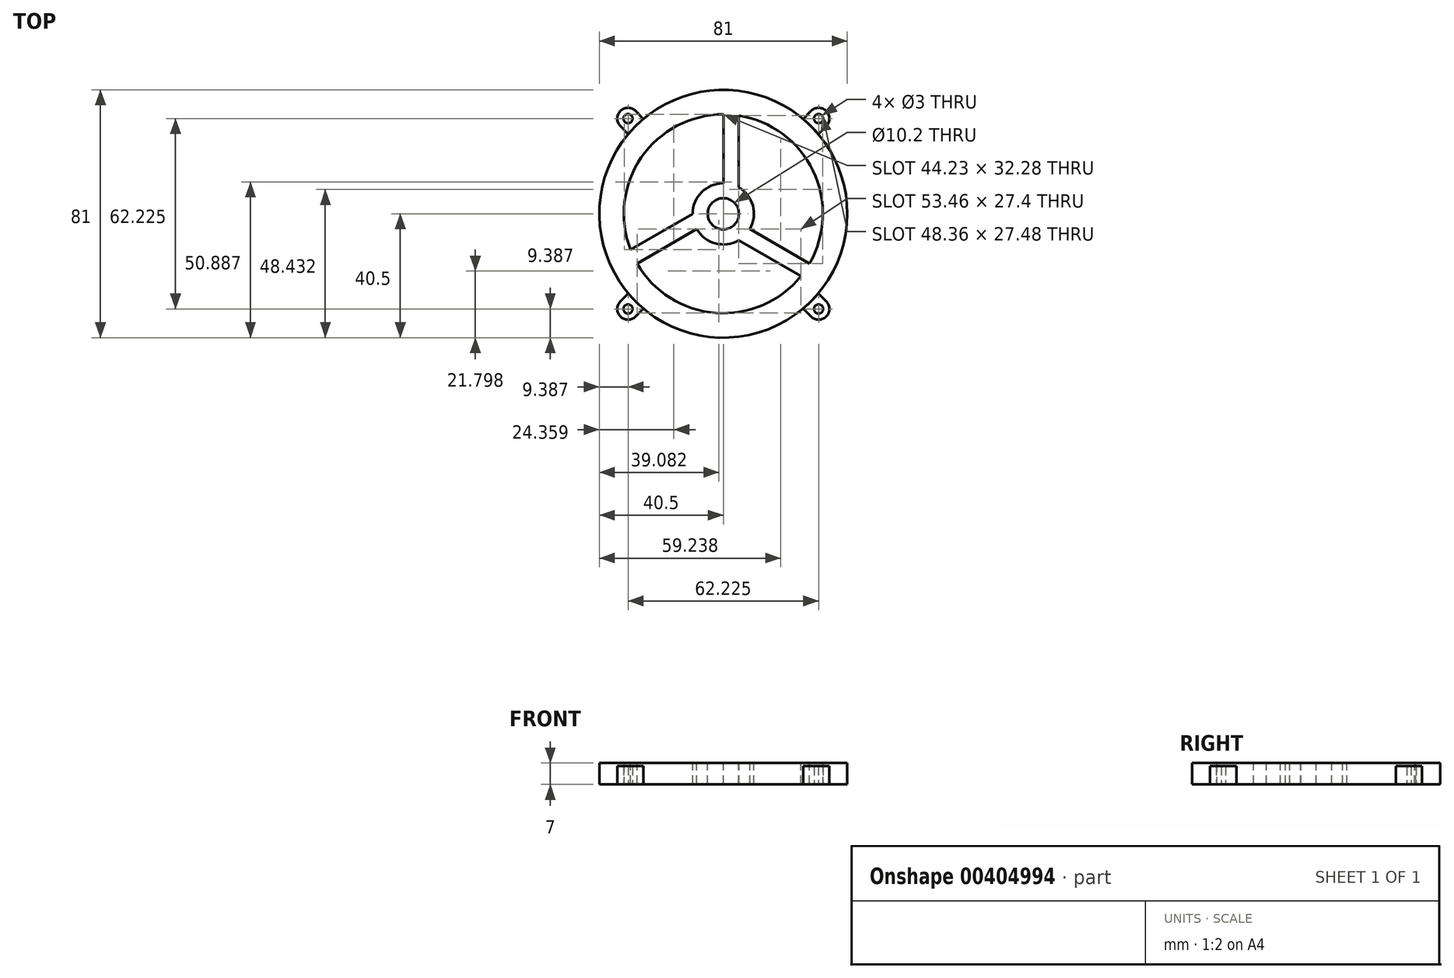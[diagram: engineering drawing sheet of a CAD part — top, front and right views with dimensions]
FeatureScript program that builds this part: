
annotation { "Feature Type Name" : "Feature", "Feature Type Description" : "" }
export const myFeature = defineFeature(function(context is Context, id is Id, definition is map)
    precondition{}
    {
        {
            var Q0;
            Q0=qCreatedBy(makeId("Top.planeOp"),FACE);
            var sketch = newSketch(context, id + "F0", { "sketchPlane" : qUnion([Q0])});
            skCircle(sketch, "E0", {"center": v(0, 0) * mm, "radius": 37 * mm});
            skCircle(sketch, "E1", {"center": v(0, 0) * mm, "radius": 32.5 * mm});
            skCircle(sketch, "E2", {"center": v(0, 0) * mm, "radius": 40.5 * mm});
            skLineSegment(sketch, "E3", {"start": v(0, 0) * mm, "end": v(-31.11, 31.11) * mm, "construction": true});
            skCircle(sketch, "E4", {"center": v(-31.11, 31.11) * mm, "radius": 1.5 * mm});
            skArc(sketch, "E5", {"start": v(-28.64, 33.59) * mm, "mid": v(-33.59, 33.59) * mm, "end": v(-33.59, 28.64) * mm});
            skLineSegment(sketch, "E6", {"start": v(-33.59, 28.64) * mm, "end": v(-31, 26.06) * mm});
            skLineSegment(sketch, "E7", {"start": v(-28.64, 33.59) * mm, "end": v(-26.06, 31) * mm});
            skLineSegment(sketch, "E8.1.0", {"start": v(-33.59, -28.64) * mm, "end": v(-31, -26.06) * mm});
            skCircle(sketch, "E8.1.1", {"center": v(-31.11, -31.11) * mm, "radius": 1.5 * mm});
            skArc(sketch, "E8.1.2", {"start": v(-33.59, -28.64) * mm, "mid": v(-33.59, -33.59) * mm, "end": v(-28.64, -33.59) * mm});
            skLineSegment(sketch, "E8.1.3", {"start": v(-28.64, -33.59) * mm, "end": v(-26.06, -31) * mm});
            skLineSegment(sketch, "E8.2.0", {"start": v(28.64, -33.59) * mm, "end": v(26.06, -31) * mm});
            skCircle(sketch, "E8.2.1", {"center": v(31.11, -31.11) * mm, "radius": 1.5 * mm});
            skArc(sketch, "E8.2.2", {"start": v(28.64, -33.59) * mm, "mid": v(33.59, -33.59) * mm, "end": v(33.59, -28.64) * mm});
            skLineSegment(sketch, "E8.2.3", {"start": v(33.59, -28.64) * mm, "end": v(31, -26.06) * mm});
            skLineSegment(sketch, "E8.3.0", {"start": v(33.59, 28.64) * mm, "end": v(31, 26.06) * mm});
            skCircle(sketch, "E8.3.1", {"center": v(31.11, 31.11) * mm, "radius": 1.5 * mm});
            skArc(sketch, "E8.3.2", {"start": v(33.59, 28.64) * mm, "mid": v(33.59, 33.59) * mm, "end": v(28.64, 33.59) * mm});
            skLineSegment(sketch, "E8.3.3", {"start": v(28.64, 33.59) * mm, "end": v(26.06, 31) * mm});
            skSolve(sketch);
        }
        {
            var Q0;
            Q0=makeQuery(id+"F0.imprint","IMPRINT",FACE,{"disambiguationData":[TD([[makeQuery(id+"F0.imprint","IMPRINT",EDGE,{"derivedFrom":sQuery(id+"F0.wireOp",EDGE,"E0")}),-1.0]])]});
            extrude(context, id + "F1", {"entities" : qUnion([Q0]), "depth" : 7 * mm});
        }
        {
            var Q0;
            {var subQ0=sQuery(id+"F0.wireOp",EDGE,"E8.1.0");Q0=makeQuery(id+"F0.imprint","IMPRINT",FACE,{"disambiguationData":[TD([[makeQuery(id+"F0.imprint","IMPRINT",EDGE,{"derivedFrom":subQ0}),-1.0]])]});}
            var Q1;
            {var subQ1=sQuery(id+"F0.wireOp",EDGE,"E8.2.0");Q1=makeQuery(id+"F0.imprint","IMPRINT",FACE,{"disambiguationData":[TD([[makeQuery(id+"F0.imprint","IMPRINT",EDGE,{"derivedFrom":subQ1}),-1.0]])]});}
            var Q2;
            {var subQ0=sQuery(id+"F0.wireOp",EDGE,"E8.3.0");Q2=makeQuery(id+"F0.imprint","IMPRINT",FACE,{"disambiguationData":[TD([[makeQuery(id+"F0.imprint","IMPRINT",EDGE,{"derivedFrom":subQ0}),-1.0]])]});}
            var Q3;
            Q3=makeQuery(id+"F0.imprint","IMPRINT",FACE,{"disambiguationData":[TD([[makeQuery(id+"F0.imprint","IMPRINT",EDGE,{"derivedFrom":sQuery(id+"F0.wireOp",EDGE,"E4")}),-1.0]])]});
            extrude(context, id + "F2", {"entities" : qUnion([Q0, Q1, Q2, Q3]), "operationType" : NewBodyOperationType.ADD, "depth" : 6 * mm});
        }
        {
            var Q0;
            Q0=makeQuery(id+"F0.imprint","IMPRINT",FACE,{"disambiguationData":[TD([[makeQuery(id+"F0.imprint","IMPRINT",EDGE,{"derivedFrom":sQuery(id+"F0.wireOp",EDGE,"E0")}),1.0]])]});
            extrude(context, id + "F3", {"entities" : qUnion([Q0]), "operationType" : NewBodyOperationType.ADD, "depth" : 7 * mm});
        }
        {
            var Q0;
            Q0=makeQuery(id+"F3.opExtrude","CAP_FACE",FACE,{"disambiguationData":[OSD([sQuery(id+"F0.wireOp",EDGE,"E0"),sQuery(id+"F0.wireOp",EDGE,"E1")])],"isStart":false});
            var sketch = newSketch(context, id + "F4", { "sketchPlane" : qUnion([Q0])});
            skCircle(sketch, "E9", {"center": v(0, 0) * mm, "radius": 5.1 * mm});
            skCircle(sketch, "E10", {"center": v(0, 0) * mm, "radius": 10 * mm});
            skLineSegment(sketch, "E11", {"start": v(0, 0) * mm, "end": v(0, 32.5) * mm});
            skLineSegment(sketch, "E12.1.0", {"start": v(0, 0) * mm, "end": v(-28.15, -16.25) * mm});
            skLineSegment(sketch, "E12.2.0", {"start": v(0, 0) * mm, "end": v(28.15, -16.25) * mm});
            skLineSegment(sketch, "E13.0", {"start": v(5, 0) * mm, "end": v(5, 32.5) * mm});
            skLineSegment(sketch, "E14.0", {"start": v(-2.5, -4.33) * mm, "end": v(25.65, -20.58) * mm});
            skLineSegment(sketch, "E15.0", {"start": v(-2.5, 4.33) * mm, "end": v(-30.65, -11.92) * mm});
            skSolve(sketch);
        }
        {
            var Q0;
            {var subQ0=sQuery(id+"F4.wireOp",EDGE,"E11");var subQ1=sQuery(id+"F4.wireOp",EDGE,"E10");var subQ2=makeQuery(id+"F4.imprint","INTERSECT",VERTEX,{"derivedFrom":[subQ1,subQ0]});Q0=makeQuery(id+"F4.imprint","IMPRINT",FACE,{"disambiguationData":[TD([[makeQuery(id+"F4.imprint","IMPRINT",EDGE,{"disambiguationData":[TD([[subQ2,1.0]])],"derivedFrom":subQ1}),-1.0]])]});}
            var Q1;
            {var subQ0=sQuery(id+"F4.wireOp",EDGE,"E13.0");var subQ1=sQuery(id+"F4.wireOp",EDGE,"E9");var subQ2=makeQuery(id+"F4.imprint","INTERSECT",VERTEX,{"derivedFrom":[subQ1,subQ0]});Q1=makeQuery(id+"F4.imprint","IMPRINT",FACE,{"disambiguationData":[TD([[makeQuery(id+"F4.imprint","IMPRINT",EDGE,{"disambiguationData":[TD([[subQ2,1.0]])],"derivedFrom":subQ1}),-1.0]])]});}
            var Q2;
            {var subQ0=sQuery(id+"F4.wireOp",EDGE,"E13.0");var subQ1=sQuery(id+"F4.wireOp",EDGE,"E9");var subQ2=makeQuery(id+"F4.imprint","INTERSECT",VERTEX,{"derivedFrom":[subQ1,subQ0]});Q2=makeQuery(id+"F4.imprint","IMPRINT",FACE,{"disambiguationData":[TD([[makeQuery(id+"F4.imprint","IMPRINT",EDGE,{"disambiguationData":[TD([[subQ2,-1.0]])],"derivedFrom":subQ1}),-1.0]])]});}
            var Q3;
            {var subQ0=sQuery(id+"F4.wireOp",EDGE,"E15.0");var subQ1=sQuery(id+"F4.wireOp",EDGE,"E9");var subQ2=makeQuery(id+"F4.imprint","INTERSECT",VERTEX,{"derivedFrom":[subQ1,subQ0]});Q3=makeQuery(id+"F4.imprint","IMPRINT",FACE,{"disambiguationData":[TD([[makeQuery(id+"F4.imprint","IMPRINT",EDGE,{"disambiguationData":[TD([[subQ2,1.0]])],"derivedFrom":subQ1}),-1.0]])]});}
            var Q4;
            {var subQ0=sQuery(id+"F4.wireOp",EDGE,"E15.0");var subQ1=sQuery(id+"F4.wireOp",EDGE,"E9");var subQ2=makeQuery(id+"F4.imprint","INTERSECT",VERTEX,{"derivedFrom":[subQ1,subQ0]});Q4=makeQuery(id+"F4.imprint","IMPRINT",FACE,{"disambiguationData":[TD([[makeQuery(id+"F4.imprint","IMPRINT",EDGE,{"disambiguationData":[TD([[subQ2,-1.0]])],"derivedFrom":subQ1}),-1.0]])]});}
            var Q5;
            {var subQ0=sQuery(id+"F4.wireOp",EDGE,"E14.0");var subQ1=sQuery(id+"F4.wireOp",EDGE,"E9");var subQ2=makeQuery(id+"F4.imprint","INTERSECT",VERTEX,{"derivedFrom":[subQ1,subQ0]});Q5=makeQuery(id+"F4.imprint","IMPRINT",FACE,{"disambiguationData":[TD([[makeQuery(id+"F4.imprint","IMPRINT",EDGE,{"disambiguationData":[TD([[subQ2,1.0]])],"derivedFrom":subQ1}),-1.0]])]});}
            var Q6;
            {var subQ0=sQuery(id+"F4.wireOp",EDGE,"E14.0");var subQ1=sQuery(id+"F4.wireOp",EDGE,"E9");var subQ2=makeQuery(id+"F4.imprint","INTERSECT",VERTEX,{"derivedFrom":[subQ1,subQ0]});Q6=makeQuery(id+"F4.imprint","IMPRINT",FACE,{"disambiguationData":[TD([[makeQuery(id+"F4.imprint","IMPRINT",EDGE,{"disambiguationData":[TD([[subQ2,-1.0]])],"derivedFrom":subQ1}),-1.0]])]});}
            var Q7;
            {var subQ0=sQuery(id+"F4.wireOp",EDGE,"E14.0");var subQ1=sQuery(id+"F4.wireOp",EDGE,"E10");var subQ2=makeQuery(id+"F4.imprint","INTERSECT",VERTEX,{"derivedFrom":[subQ1,subQ0]});Q7=makeQuery(id+"F4.imprint","IMPRINT",FACE,{"disambiguationData":[TD([[makeQuery(id+"F4.imprint","IMPRINT",EDGE,{"disambiguationData":[TD([[subQ2,-1.0]])],"derivedFrom":subQ1}),-1.0]])]});}
            var Q8;
            {var subQ0=sQuery(id+"F4.wireOp",EDGE,"E15.0");var subQ1=sQuery(id+"F4.wireOp",EDGE,"E10");var subQ2=makeQuery(id+"F4.imprint","INTERSECT",VERTEX,{"derivedFrom":[subQ1,subQ0]});Q8=makeQuery(id+"F4.imprint","IMPRINT",FACE,{"disambiguationData":[TD([[makeQuery(id+"F4.imprint","IMPRINT",EDGE,{"disambiguationData":[TD([[subQ2,-1.0]])],"derivedFrom":subQ1}),-1.0]])]});}
            extrude(context, id + "F5", {"entities" : qUnion([Q0, Q1, Q2, Q3, Q4, Q5, Q6, Q7, Q8]), "operationType" : NewBodyOperationType.ADD, "oppositeDirection" : true, "depth" : 7 * mm});
        }
    });
